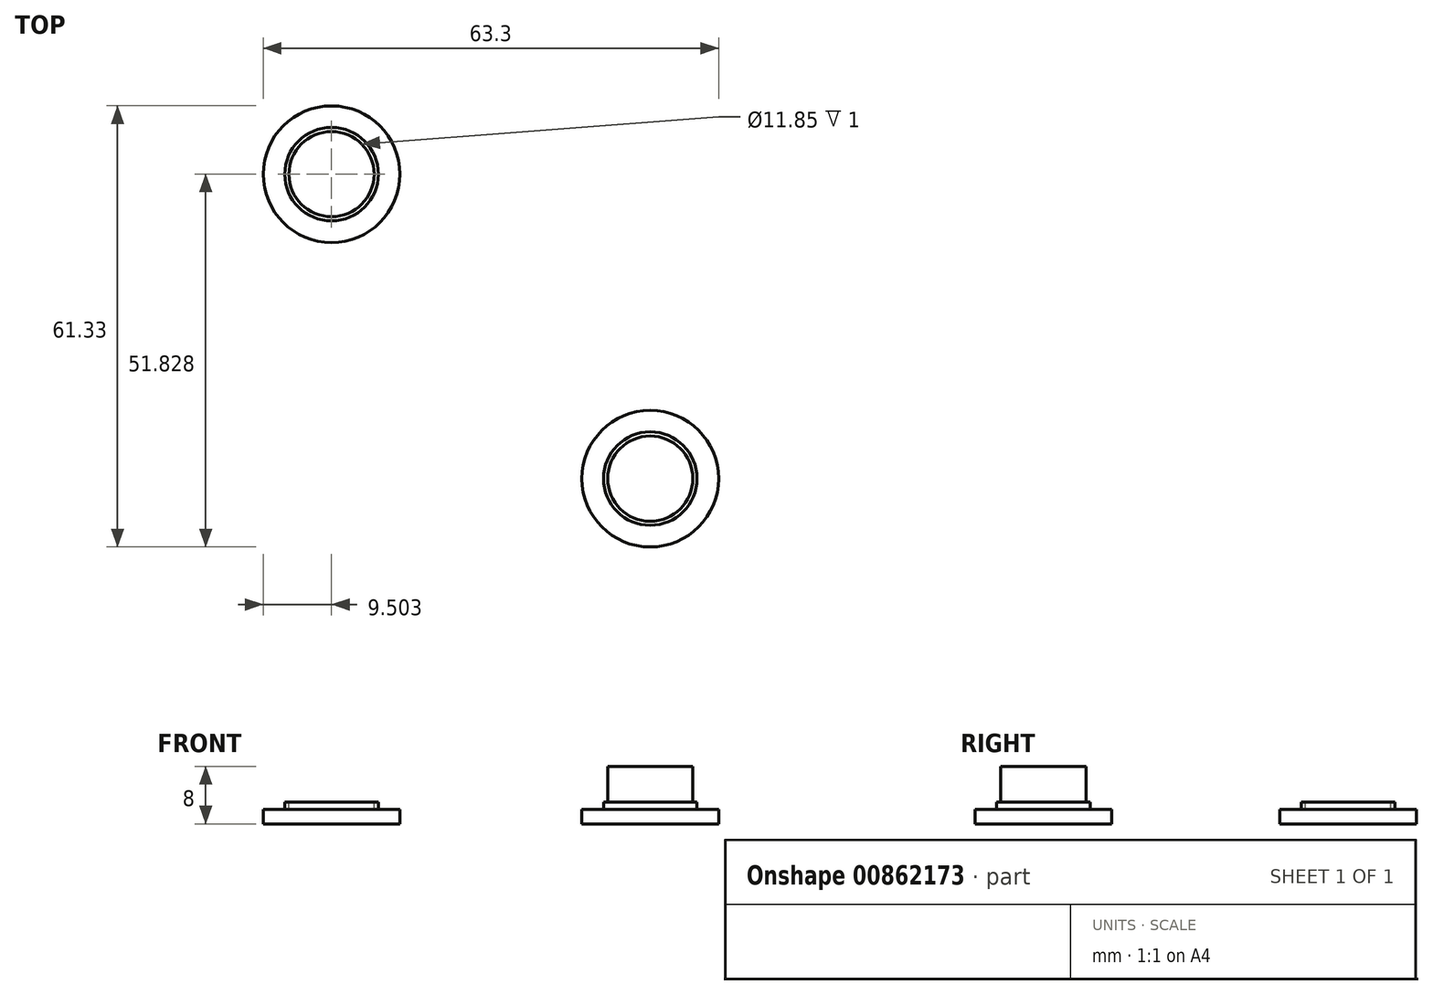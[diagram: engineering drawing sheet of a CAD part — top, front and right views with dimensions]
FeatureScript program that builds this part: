
annotation { "Feature Type Name" : "Feature", "Feature Type Description" : "" }
export const myFeature = defineFeature(function(context is Context, id is Id, definition is map)
    precondition{}
    {
        {
            var Q0;
            Q0=qCreatedBy(makeId("Top.planeOp"),FACE);
            var sketch = newSketch(context, id + "F0", { "sketchPlane" : qUnion([Q0])});
            skCircle(sketch, "E0", {"center": v(0, 0) * mm, "radius": 9.5 * mm});
            skSolve(sketch);
        }
        {
            var Q0;
            Q0=makeQuery(id+"F0.imprint","IMPRINT",FACE,{"disambiguationData":[TD([[makeQuery(id+"F0.imprint","IMPRINT",EDGE,{"derivedFrom":sQuery(id+"F0.wireOp",EDGE,"E0")}),1.0]])]});
            extrude(context, id + "F1", {"entities" : qUnion([Q0]), "depth" : 2 * mm, "offsetDistance" : 25 * mm});
        }
        {
            var Q0;
            Q0=makeQuery(id+"F1.opExtrude","CAP_FACE",FACE,{"disambiguationData":[OSD([sQuery(id+"F0.wireOp",EDGE,"E0")])],"isStart":false});
            var sketch = newSketch(context, id + "F2", { "sketchPlane" : qUnion([Q0])});
            skCircle(sketch, "E1", {"center": v(0, 0) * mm, "radius": 6.5 * mm});
            skSolve(sketch);
        }
        {
            var Q0;
            Q0=makeQuery(id+"F2.imprint","IMPRINT",FACE,{"disambiguationData":[TD([[makeQuery(id+"F2.imprint","IMPRINT",EDGE,{"derivedFrom":sQuery(id+"F2.wireOp",EDGE,"E1")}),1.0]])]});
            extrude(context, id + "F3", {"entities" : qUnion([Q0]), "operationType" : NewBodyOperationType.ADD, "depth" : 1 * mm, "offsetDistance" : 25 * mm});
        }
        {
            var Q0;
            Q0=makeQuery(id+"F3.opExtrude","CAP_FACE",FACE,{"disambiguationData":[OSD([sQuery(id+"F2.wireOp",EDGE,"E1")])],"isStart":false});
            var sketch = newSketch(context, id + "F4", { "sketchPlane" : qUnion([Q0])});
            skCircle(sketch, "E2", {"center": v(0, 0) * mm, "radius": 5.92 * mm});
            skSolve(sketch);
        }
        {
            var Q0;
            Q0 = qSketchRegion(id + "F4", true);
            extrude(context, id + "F5", {"entities" : qUnion([Q0]), "operationType" : NewBodyOperationType.ADD, "depth" : 5 * mm, "offsetDistance" : 25 * mm});
        }
        {
            var Q0;
            Q0=qCreatedBy(makeId("Top.planeOp"),FACE);
            var sketch = newSketch(context, id + "F6", { "sketchPlane" : qUnion([Q0])});
            skCircle(sketch, "E3", {"center": v(-44.3, 42.33) * mm, "radius": 9.5 * mm});
            skSolve(sketch);
        }
        {
            var Q0;
            Q0=makeQuery(id+"F6.imprint","IMPRINT",FACE,{"disambiguationData":[TD([[makeQuery(id+"F6.imprint","IMPRINT",EDGE,{"derivedFrom":sQuery(id+"F6.wireOp",EDGE,"E3")}),1.0]])]});
            extrude(context, id + "F7", {"entities" : qUnion([Q0]), "depth" : 2 * mm, "offsetDistance" : 25 * mm});
        }
        {
            var Q0;
            Q0=makeQuery(id+"F7.opExtrude","CAP_FACE",FACE,{"disambiguationData":[OSD([sQuery(id+"F6.wireOp",EDGE,"E3")])],"isStart":false});
            var sketch = newSketch(context, id + "F8", { "sketchPlane" : qUnion([Q0])});
            skCircle(sketch, "E4", {"center": v(-44.3, 42.33) * mm, "radius": 6.5 * mm});
            skSolve(sketch);
        }
        {
            var Q0;
            Q0=makeQuery(id+"F8.imprint","IMPRINT",FACE,{"disambiguationData":[TD([[makeQuery(id+"F8.imprint","IMPRINT",EDGE,{"derivedFrom":sQuery(id+"F8.wireOp",EDGE,"E4")}),1.0]])]});
            extrude(context, id + "F9", {"entities" : qUnion([Q0]), "operationType" : NewBodyOperationType.ADD, "depth" : 1 * mm, "offsetDistance" : 25 * mm});
        }
        {
            var Q0;
            Q0=makeQuery(id+"F9.opExtrude","CAP_FACE",FACE,{"disambiguationData":[OSD([sQuery(id+"F8.wireOp",EDGE,"E4")])],"isStart":false});
            var sketch = newSketch(context, id + "F10", { "sketchPlane" : qUnion([Q0])});
            skCircle(sketch, "E5", {"center": v(-44.3, 42.33) * mm, "radius": 5.93 * mm});
            skSolve(sketch);
        }
        {
            var Q0;
            Q0=makeQuery(id+"F10.imprint","IMPRINT",FACE,{"disambiguationData":[TD([[makeQuery(id+"F10.imprint","IMPRINT",EDGE,{"derivedFrom":sQuery(id+"F10.wireOp",EDGE,"E5")}),1.0]])]});
            extrude(context, id + "F11", {"entities" : qUnion([Q0]), "operationType" : NewBodyOperationType.REMOVE, "oppositeDirection" : true, "depth" : 1 * mm, "offsetDistance" : 25 * mm});
        }
    });
